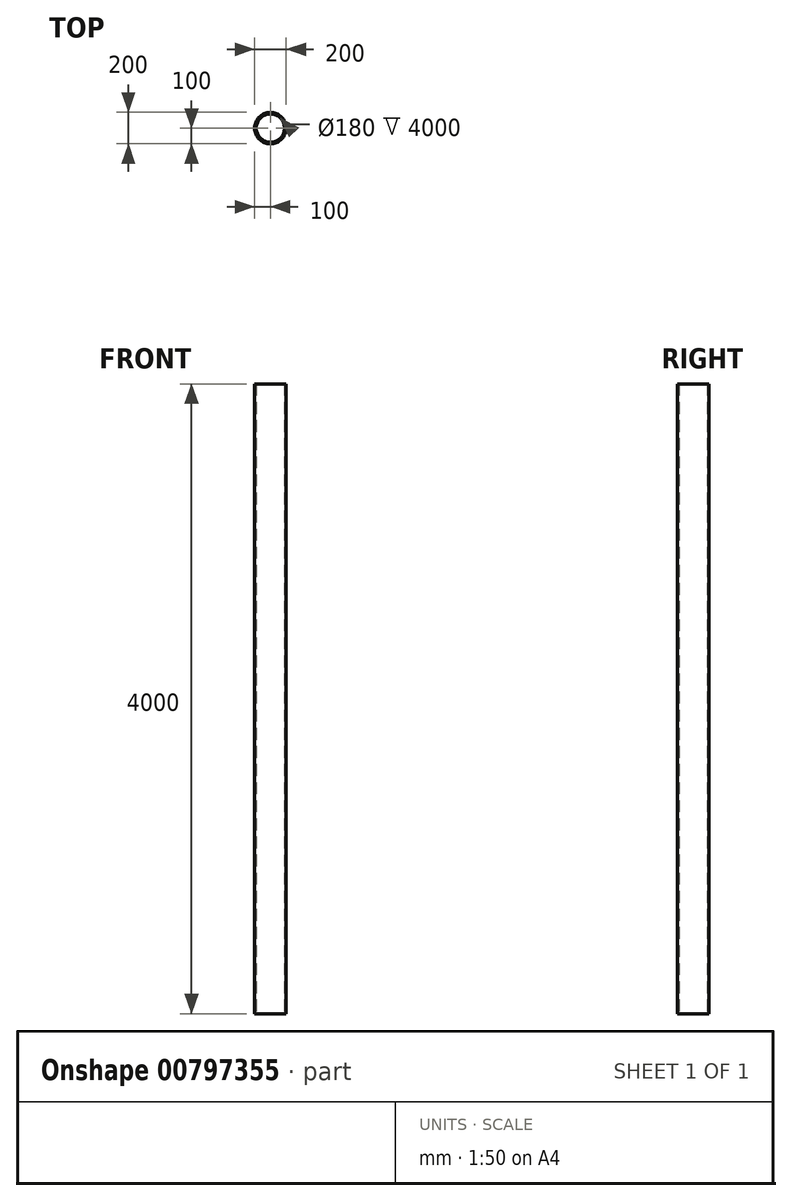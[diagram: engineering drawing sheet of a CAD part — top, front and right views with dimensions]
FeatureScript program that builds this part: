
annotation { "Feature Type Name" : "Feature", "Feature Type Description" : "" }
export const myFeature = defineFeature(function(context is Context, id is Id, definition is map)
    precondition{}
    {
        {
            var Q0;
            Q0=qCreatedBy(makeId("Top.planeOp"),FACE);
            var sketch = newSketch(context, id + "F0", { "sketchPlane" : qUnion([Q0])});
            skCircle(sketch, "E0", {"center": v(0, 0) * mm, "radius": 90 * mm});
            skCircle(sketch, "E1", {"center": v(0, 0) * mm, "radius": 100 * mm});
            skSolve(sketch);
        }
        {
            var Q0;
            Q0=makeQuery(id+"F0.imprint","IMPRINT",FACE,{"disambiguationData":[TD([[makeQuery(id+"F0.imprint","IMPRINT",EDGE,{"derivedFrom":sQuery(id+"F0.wireOp",EDGE,"E0")}),-1.0]])]});
            extrude(context, id + "F1", {"entities" : qUnion([Q0]), "depth" : 4000 * mm, "offsetDistance" : 25 * mm});
        }
    });
